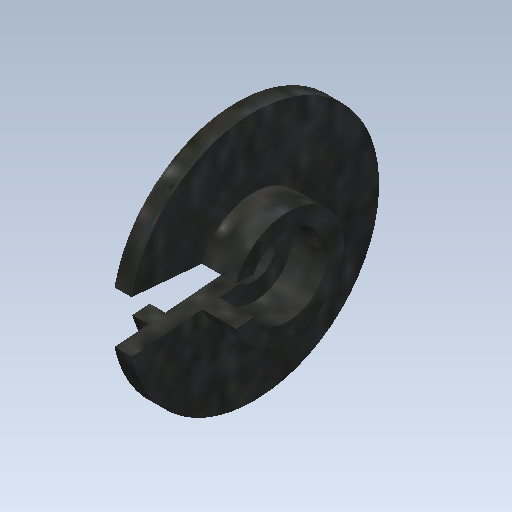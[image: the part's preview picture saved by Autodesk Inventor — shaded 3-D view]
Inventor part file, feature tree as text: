
AUTODESK INVENTOR PART (.ipt)
format: ipt  version: 2020 (Build 240168000, 168)  size: 190,976 bytes
history: native  units: mm
features: sketch x2, revolve x1, extrude x1
ambient origin geometry x8: Origin, YZ Plane, XZ Plane, XY Plane, X Axis, Y Axis, Z Axis, Center Point
bodies: Body1 (feature_tree)
feature tree (4):
  revolve  "Revolution2"  [1 undecoded]
  extrude  "Extrusion1"  Depth=1.65mm
  sketch  "Sketch1"  dims[d0=5.1mm d1=4.25mm]
  sketch  "Sketch2"  dims[d2=3.0mm d3=1.65mm d4=1.3mm d5=2.5mm d6=0.0mm d7=9.55mm d8=7.0mm d9=5.7mm d11=90.0deg d12=0.872665mm d13=0.872665mm d14=2.5mm d15=1.25mm d16=10.0mm d17=0.0mm]
note: 1 required parameter value undecoded (feature->parameter linkage not recoverable at this tier; creation-order binding heuristic only, values carry confidence <= 0.55)
